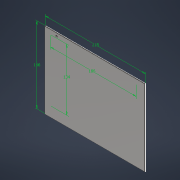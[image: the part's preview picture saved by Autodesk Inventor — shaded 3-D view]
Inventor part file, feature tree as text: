
AUTODESK INVENTOR PART (.ipt)
format: ipt  version: 2022 (Build 260153070, 153G)  size: 117,248 bytes
history: native  units: mm
features: sketch x2, other x1, extrude x1, chamfer x1, hole x1
ambient origin geometry x8: Origin, YZ Plane, XZ Plane, XY Plane, X Axis, Y Axis, Z Axis, Center Point
bodies: Body1 (feature_tree)
feature tree (6):
  other  "Твердое тело1"
  sketch  "Эскиз1"
  extrude  "Выдавливание1"  Depth=218.0mm
  chamfer  "Фаска1"  Distance=166.0mm
  hole  "Отверстие1"  [1 undecoded]
  sketch  "Эскиз2"
note: 1 required parameter value undecoded (feature->parameter linkage not recoverable at this tier; creation-order binding heuristic only, values carry confidence <= 0.55)
